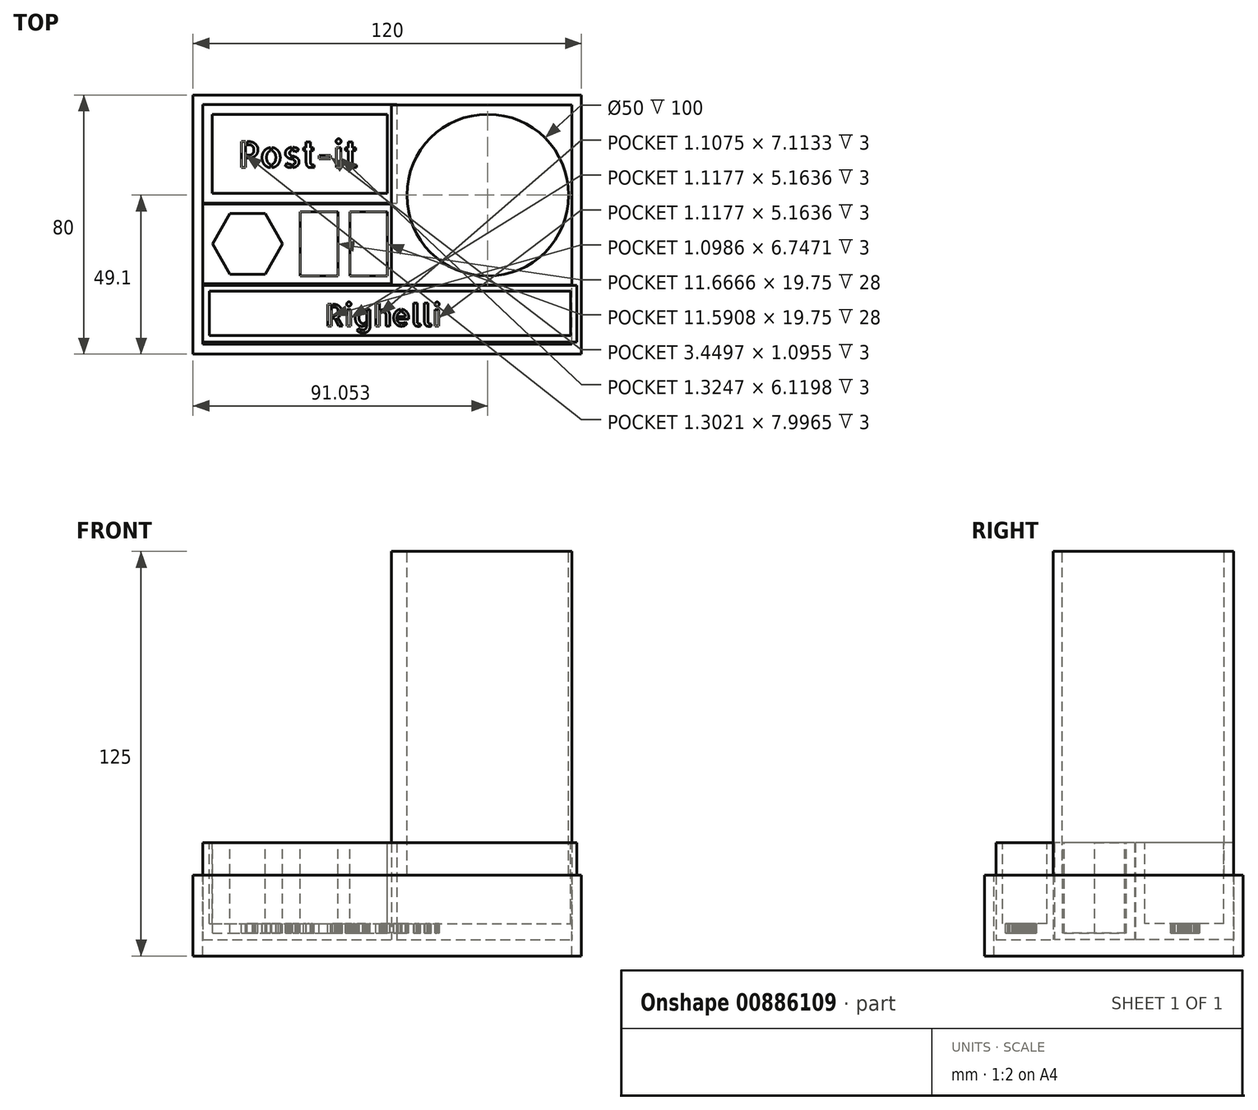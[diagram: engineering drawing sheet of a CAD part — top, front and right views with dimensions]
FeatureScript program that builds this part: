
annotation { "Feature Type Name" : "Feature", "Feature Type Description" : "" }
export const myFeature = defineFeature(function(context is Context, id is Id, definition is map)
    precondition{}
    {
        {
            var Q0;
            Q0=qCreatedBy(makeId("Top.planeOp"),FACE);
            var sketch = newSketch(context, id + "F0", { "sketchPlane" : qUnion([Q0])});
            skLineSegment(sketch, "E0.bottom", {"start": v(-60, 40) * mm, "end": v(60, 40) * mm});
            skLineSegment(sketch, "E0.top", {"start": v(-60, -40) * mm, "end": v(60, -40) * mm});
            skLineSegment(sketch, "E0.left", {"start": v(-60, 40) * mm, "end": v(-60, -40) * mm});
            skLineSegment(sketch, "E0.right", {"start": v(60, 40) * mm, "end": v(60, -40) * mm});
            skSolve(sketch);
        }
        {
            var Q0;
            Q0=qSketchRegion(id+"F0",true);
            extrude(context, id + "F1", {"entities" : qUnion([Q0]), "depth" : 25 * mm, "offsetDistance" : 25 * mm});
        }
        {
            var Q0;
            Q0=makeQuery(id+"F1.opExtrude","CAP_FACE",FACE,{"disambiguationData":[OSD([sQuery(id+"F0.wireOp",EDGE,"E0.bottom"),sQuery(id+"F0.wireOp",EDGE,"E0.top"),sQuery(id+"F0.wireOp",EDGE,"E0.left"),sQuery(id+"F0.wireOp",EDGE,"E0.right")])],"isStart":false});
            var sketch = newSketch(context, id + "F2", { "sketchPlane" : qUnion([Q0])});
            skLineSegment(sketch, "E1.bottom", {"start": v(-57, 37) * mm, "end": v(57, 37) * mm});
            skLineSegment(sketch, "E1.top", {"start": v(-57, -37) * mm, "end": v(57, -37) * mm});
            skLineSegment(sketch, "E1.left", {"start": v(-57, 37) * mm, "end": v(-57, -37) * mm});
            skLineSegment(sketch, "E1.right", {"start": v(57, 37) * mm, "end": v(57, -37) * mm});
            skSolve(sketch);
        }
        {
            var Q0;
            Q0=makeQuery(id+"F2.imprint","IMPRINT",FACE,{"disambiguationData":[TD([[makeQuery(id+"F2.imprint","IMPRINT",EDGE,{"derivedFrom":sQuery(id+"F2.wireOp",EDGE,"E1.bottom")}),-1.0]])]});
            extrude(context, id + "F3", {"entities" : qUnion([Q0]), "operationType" : NewBodyOperationType.REMOVE, "oppositeDirection" : true, "depth" : 20 * mm, "offsetDistance" : 25 * mm});
        }
        {
            var Q0;
            Q0=makeQuery(id+"F3.boolean.opBoolean","COPY",FACE,{"derivedFrom":makeQuery(id+"F3.opExtrude","CAP_FACE",FACE,{"disambiguationData":[OSD([sQuery(id+"F2.wireOp",EDGE,"E1.bottom"),sQuery(id+"F2.wireOp",EDGE,"E1.top"),sQuery(id+"F2.wireOp",EDGE,"E1.left"),sQuery(id+"F2.wireOp",EDGE,"E1.right")])],"isStart":false})});
            var sketch = newSketch(context, id + "F4", { "sketchPlane" : qUnion([Q0])});
            skLineSegment(sketch, "E2.bottom", {"start": v(57, 37) * mm, "end": v(1.35, 37) * mm});
            skLineSegment(sketch, "E2.top", {"start": v(57, -18.68) * mm, "end": v(1.35, -18.68) * mm});
            skLineSegment(sketch, "E2.left", {"start": v(57, 37) * mm, "end": v(57, -18.68) * mm});
            skLineSegment(sketch, "E2.right", {"start": v(1.35, 37) * mm, "end": v(1.35, -18.68) * mm});
            skSolve(sketch);
        }
        {
            var Q0;
            Q0=makeQuery(id+"F4.imprint","IMPRINT",FACE,{"disambiguationData":[TD([[makeQuery(id+"F4.imprint","IMPRINT",EDGE,{"derivedFrom":sQuery(id+"F4.wireOp",EDGE,"E2.bottom")}),-1.0]])]});
            var sketch = newSketch(context, id + "F5", { "sketchPlane" : qUnion([Q0])});
            skSolve(sketch);
        }
        {
            var Q0;
            Q0=makeQuery(id+"F5.imprint","IMPRINT",FACE,{"disambiguationData":[TD([[makeQuery(id+"F5.imprint","IMPRINT",EDGE,{"derivedFrom":makeQuery(id+"F4.imprint","IMPRINT",EDGE,{"derivedFrom":sQuery(id+"F4.wireOp",EDGE,"E2.bottom")})}),-1.0]])]});
            extrude(context, id + "F6", {"entities" : qUnion([Q0]), "operationType" : NewBodyOperationType.ADD, "depth" : 120 * mm, "offsetDistance" : 25 * mm});
        }
        {
            var Q0;
            Q0=makeQuery(id+"F6.opExtrude","CAP_FACE",FACE,{"disambiguationData":[OSD([sQuery(id+"F4.wireOp",EDGE,"E2.bottom"),sQuery(id+"F4.wireOp",EDGE,"E2.top"),sQuery(id+"F4.wireOp",EDGE,"E2.left"),sQuery(id+"F4.wireOp",EDGE,"E2.right")])],"isStart":false});
            var sketch = newSketch(context, id + "F7", { "sketchPlane" : qUnion([Q0])});
            skCircle(sketch, "E3", {"center": v(31.05, 9.1) * mm, "radius": 25 * mm});
            skSolve(sketch);
        }
        {
            var Q0;
            Q0=qSketchRegion(id+"F2",true);
            var Q1;
            Q1=qSketchRegion(id+"F7",true);
            extrude(context, id + "F8", {"entities" : qUnion([Q0, Q1]), "operationType" : NewBodyOperationType.REMOVE, "oppositeDirection" : true, "depth" : 116 * mm, "offsetDistance" : 25 * mm});
        }
        {
            var Q0;
            {var subQ4=sQuery(id+"F4.wireOp",EDGE,"E2.top");Q0=makeQuery(id+"F4.imprint","IMPRINT",FACE,{"disambiguationData":[TD([[makeQuery(id+"F4.imprint","IMPRINT",EDGE,{"derivedFrom":subQ4}),1.0]])]});}
            var sketch = newSketch(context, id + "F9", { "sketchPlane" : qUnion([Q0])});
            skLineSegment(sketch, "E4.bottom", {"start": v(-57.04, 37.04) * mm, "end": v(2.94, 37.04) * mm});
            skLineSegment(sketch, "E4.top", {"start": v(-57.04, 6.65) * mm, "end": v(2.94, 6.65) * mm});
            skLineSegment(sketch, "E4.left", {"start": v(-57.04, 37.04) * mm, "end": v(-57.04, 6.65) * mm});
            skLineSegment(sketch, "E4.right", {"start": v(2.94, 37.04) * mm, "end": v(2.94, 6.65) * mm});
            skSolve(sketch);
        }
        {
            var Q0;
            Q0=qSketchRegion(id+"F9",true);
            extrude(context, id + "F10", {"entities" : qUnion([Q0]), "depth" : 30 * mm, "offsetDistance" : 25 * mm});
        }
        {
            var Q0;
            Q0=makeQuery(id+"F10.opExtrude","CAP_FACE",FACE,{"disambiguationData":[OSD([sQuery(id+"F9.wireOp",EDGE,"E4.bottom"),sQuery(id+"F9.wireOp",EDGE,"E4.top"),sQuery(id+"F9.wireOp",EDGE,"E4.left"),sQuery(id+"F9.wireOp",EDGE,"E4.right")])],"isStart":false});
            var sketch = newSketch(context, id + "F11", { "sketchPlane" : qUnion([Q0])});
            skLineSegment(sketch, "E5.bottom", {"start": v(-54.04, 34.04) * mm, "end": v(0, 34.04) * mm});
            skLineSegment(sketch, "E5.top", {"start": v(-54.04, 9.65) * mm, "end": v(0, 9.65) * mm});
            skLineSegment(sketch, "E5.left", {"start": v(-54.04, 34.04) * mm, "end": v(-54.04, 9.65) * mm});
            skLineSegment(sketch, "E5.right", {"start": v(0, 34.04) * mm, "end": v(0, 9.65) * mm});
            skSolve(sketch);
        }
        {
            var Q0;
            Q0=makeQuery(id+"F11.imprint","IMPRINT",FACE,{"disambiguationData":[TD([[makeQuery(id+"F11.imprint","IMPRINT",EDGE,{"derivedFrom":sQuery(id+"F11.wireOp",EDGE,"E5.bottom")}),-1.0]])]});
            extrude(context, id + "F12", {"entities" : qUnion([Q0]), "operationType" : NewBodyOperationType.REMOVE, "oppositeDirection" : true, "depth" : 25 * mm, "offsetDistance" : 25 * mm});
        }
        {
            var Q0;
            {var subQ4=sQuery(id+"F4.wireOp",EDGE,"E2.top");Q0=makeQuery(id+"F4.imprint","IMPRINT",FACE,{"disambiguationData":[TD([[makeQuery(id+"F4.imprint","IMPRINT",EDGE,{"derivedFrom":subQ4}),1.0]])]});}
            var sketch = newSketch(context, id + "F13", { "sketchPlane" : qUnion([Q0])});
            skLineSegment(sketch, "E6.bottom", {"start": v(-57, 6.41) * mm, "end": v(1.35, 6.41) * mm});
            skLineSegment(sketch, "E6.top", {"start": v(-57, -18.34) * mm, "end": v(1.35, -18.34) * mm});
            skLineSegment(sketch, "E6.left", {"start": v(-57, 6.41) * mm, "end": v(-57, -18.34) * mm});
            skLineSegment(sketch, "E6.right", {"start": v(1.35, 6.41) * mm, "end": v(1.35, -18.34) * mm});
            skSolve(sketch);
        }
        {
            var Q0;
            Q0=qSketchRegion(id+"F13",true);
            extrude(context, id + "F14", {"entities" : qUnion([Q0]), "depth" : 30 * mm, "offsetDistance" : 25 * mm});
        }
        {
            var Q0;
            Q0=makeQuery(id+"F14.opExtrude","CAP_FACE",FACE,{"disambiguationData":[OSD([sQuery(id+"F13.wireOp",EDGE,"E6.bottom"),sQuery(id+"F13.wireOp",EDGE,"E6.top"),sQuery(id+"F13.wireOp",EDGE,"E6.left"),sQuery(id+"F13.wireOp",EDGE,"E6.right")])],"isStart":false});
            var sketch = newSketch(context, id + "F15", { "sketchPlane" : qUnion([Q0])});
            skCircle(sketch, "E7.cCircle", {"center": v(-43.17, -5.96) * mm, "radius": 9.38 * mm, "construction": true});
            skLineSegment(sketch, "E7.0", {"start": v(-48.59, 3.41) * mm, "end": v(-37.76, 3.41) * mm});
            skLineSegment(sketch, "E7.1", {"start": v(-37.76, 3.41) * mm, "end": v(-32.35, -5.96) * mm});
            skLineSegment(sketch, "E7.2", {"start": v(-32.35, -5.96) * mm, "end": v(-37.76, -15.34) * mm});
            skLineSegment(sketch, "E7.3", {"start": v(-37.76, -15.34) * mm, "end": v(-48.59, -15.34) * mm});
            skLineSegment(sketch, "E7.4", {"start": v(-48.59, -15.34) * mm, "end": v(-54, -5.96) * mm});
            skLineSegment(sketch, "E7.5", {"start": v(-54, -5.96) * mm, "end": v(-48.59, 3.41) * mm});
            skPoint(sketch, "E7.0.midPoint", {"position": v(-43.17, 3.41) * mm});
            skSolve(sketch);
        }
        {
            var Q0;
            Q0=qSketchRegion(id+"F15",true);
            extrude(context, id + "F16", {"entities" : qUnion([Q0]), "operationType" : NewBodyOperationType.REMOVE, "oppositeDirection" : true, "depth" : 28 * mm, "offsetDistance" : 25 * mm});
        }
        {
            var Q0;
            Q0=makeQuery(id+"F15.imprint","IMPRINT",FACE,{"disambiguationData":[TD([[makeQuery(id+"F15.imprint","IMPRINT",EDGE,{"derivedFrom":sQuery(id+"F15.wireOp",EDGE,"E7.0")}),-1.0]])]});
            extrude(context, id + "F17", {"entities" : qUnion([Q0]), "operationType" : NewBodyOperationType.REMOVE, "oppositeDirection" : true, "depth" : 28 * mm, "offsetDistance" : 25 * mm});
        }
        {
            var Q0;
            Q0=makeQuery(id+"F14.opExtrude","CAP_FACE",FACE,{"disambiguationData":[OSD([sQuery(id+"F13.wireOp",EDGE,"E6.bottom"),sQuery(id+"F13.wireOp",EDGE,"E6.top"),sQuery(id+"F13.wireOp",EDGE,"E6.left"),sQuery(id+"F13.wireOp",EDGE,"E6.right")])],"isStart":false});
            var sketch = newSketch(context, id + "F18", { "sketchPlane" : qUnion([Q0])});
            skLineSegment(sketch, "E8.bottom", {"start": v(-26.87, 3.91) * mm, "end": v(-15.2, 3.91) * mm});
            skLineSegment(sketch, "E8.top", {"start": v(-26.87, -15.84) * mm, "end": v(-15.2, -15.84) * mm});
            skLineSegment(sketch, "E8.left", {"start": v(-26.87, 3.91) * mm, "end": v(-26.87, -15.84) * mm});
            skLineSegment(sketch, "E8.right", {"start": v(-15.2, 3.91) * mm, "end": v(-15.2, -15.84) * mm});
            skSolve(sketch);
        }
        {
            var Q0;
            Q0=makeQuery(id+"F18.imprint","IMPRINT",FACE,{"disambiguationData":[TD([[makeQuery(id+"F18.imprint","IMPRINT",EDGE,{"derivedFrom":sQuery(id+"F18.wireOp",EDGE,"E8.bottom")}),-1.0]])]});
            extrude(context, id + "F19", {"entities" : qUnion([Q0]), "operationType" : NewBodyOperationType.REMOVE, "oppositeDirection" : true, "depth" : 28 * mm, "offsetDistance" : 25 * mm});
        }
        {
            var Q0;
            Q0=makeQuery(id+"F14.opExtrude","CAP_FACE",FACE,{"disambiguationData":[OSD([sQuery(id+"F13.wireOp",EDGE,"E6.bottom"),sQuery(id+"F13.wireOp",EDGE,"E6.top"),sQuery(id+"F13.wireOp",EDGE,"E6.left"),sQuery(id+"F13.wireOp",EDGE,"E6.right")])],"isStart":false});
            var sketch = newSketch(context, id + "F20", { "sketchPlane" : qUnion([Q0])});
            skLineSegment(sketch, "E9.bottom", {"start": v(-11.6, 3.91) * mm, "end": v(0, 3.91) * mm});
            skLineSegment(sketch, "E9.top", {"start": v(-11.6, -15.84) * mm, "end": v(0, -15.84) * mm});
            skLineSegment(sketch, "E9.left", {"start": v(-11.6, 3.91) * mm, "end": v(-11.6, -15.84) * mm});
            skLineSegment(sketch, "E9.right", {"start": v(0, 3.91) * mm, "end": v(0, -15.84) * mm});
            skSolve(sketch);
        }
        {
            var Q0;
            Q0=qSketchRegion(id+"F20",true);
            extrude(context, id + "F21", {"entities" : qUnion([Q0]), "operationType" : NewBodyOperationType.REMOVE, "oppositeDirection" : true, "depth" : 28 * mm, "offsetDistance" : 25 * mm});
        }
        {
            var Q0;
            {var subQ4=sQuery(id+"F4.wireOp",EDGE,"E2.top");Q0=makeQuery(id+"F4.imprint","IMPRINT",FACE,{"disambiguationData":[TD([[makeQuery(id+"F4.imprint","IMPRINT",EDGE,{"derivedFrom":subQ4}),1.0]])]});}
            var sketch = newSketch(context, id + "F22", { "sketchPlane" : qUnion([Q0])});
            skLineSegment(sketch, "E10.bottom", {"start": v(-57.04, -18.79) * mm, "end": v(58.61, -18.79) * mm});
            skLineSegment(sketch, "E10.top", {"start": v(-57.04, -36.34) * mm, "end": v(58.61, -36.34) * mm});
            skLineSegment(sketch, "E10.left", {"start": v(-57.04, -18.79) * mm, "end": v(-57.04, -36.34) * mm});
            skLineSegment(sketch, "E10.right", {"start": v(58.61, -18.79) * mm, "end": v(58.61, -36.34) * mm});
            skSolve(sketch);
        }
        {
            var Q0;
            Q0=qSketchRegion(id+"F22",true);
            extrude(context, id + "F23", {"entities" : qUnion([Q0]), "operationType" : NewBodyOperationType.ADD, "depth" : 30 * mm, "offsetDistance" : 25 * mm});
        }
        {
            var Q0;
            Q0=makeQuery(id+"F23.opExtrude","CAP_FACE",FACE,{"disambiguationData":[OSD([sQuery(id+"F22.wireOp",EDGE,"E10.bottom"),sQuery(id+"F22.wireOp",EDGE,"E10.top"),sQuery(id+"F22.wireOp",EDGE,"E10.left"),sQuery(id+"F22.wireOp",EDGE,"E10.right")])],"isStart":false});
            var sketch = newSketch(context, id + "F24", { "sketchPlane" : qUnion([Q0])});
            skLineSegment(sketch, "E11.bottom", {"start": v(-55.04, -20.59) * mm, "end": v(56.61, -20.59) * mm});
            skLineSegment(sketch, "E11.top", {"start": v(-55.04, -34.34) * mm, "end": v(56.61, -34.34) * mm});
            skLineSegment(sketch, "E11.left", {"start": v(-55.04, -20.59) * mm, "end": v(-55.04, -34.34) * mm});
            skLineSegment(sketch, "E11.right", {"start": v(56.61, -20.59) * mm, "end": v(56.61, -34.34) * mm});
            skSolve(sketch);
        }
        {
            var Q0;
            Q0=qSketchRegion(id+"F24",true);
            extrude(context, id + "F25", {"entities" : qUnion([Q0]), "operationType" : NewBodyOperationType.REMOVE, "oppositeDirection" : true, "depth" : 25 * mm, "offsetDistance" : 25 * mm});
        }
        {
            var Q0;
            Q0=makeQuery(id+"F25.boolean.opBoolean","COPY",FACE,{"derivedFrom":makeQuery(id+"F25.opExtrude","CAP_FACE",FACE,{"disambiguationData":[OSD([sQuery(id+"F24.wireOp",EDGE,"E11.bottom"),sQuery(id+"F24.wireOp",EDGE,"E11.top"),sQuery(id+"F24.wireOp",EDGE,"E11.left"),sQuery(id+"F24.wireOp",EDGE,"E11.right")])],"isStart":false})});
            var sketch = newSketch(context, id + "F26", { "sketchPlane" : qUnion([Q0])});
            skText(sketch, "E12", { "text": "Righelli", "fontName": "AllertaStencil-Regular.ttf"});
            const initialGuessF26  = {"E12": [-0.01924, -0.03139, 1, 0, 0.00675]};
            skSetInitialGuess(sketch, initialGuessF26);
            skSolve(sketch);
        }
        {
            var Q0;
            Q0=qSketchRegion(id+"F26",true);
            extrude(context, id + "F27", {"entities" : qUnion([Q0]), "operationType" : NewBodyOperationType.REMOVE, "oppositeDirection" : true, "depth" : 3 * mm, "offsetDistance" : 25 * mm});
        }
        {
            var Q0;
            Q0=makeQuery(id+"F12.boolean.opBoolean","COPY",FACE,{"derivedFrom":makeQuery(id+"F12.opExtrude","CAP_FACE",FACE,{"disambiguationData":[OSD([sQuery(id+"F11.wireOp",EDGE,"E5.bottom"),sQuery(id+"F11.wireOp",EDGE,"E5.top"),sQuery(id+"F11.wireOp",EDGE,"E5.left"),sQuery(id+"F11.wireOp",EDGE,"E5.right")])],"isStart":false})});
            var sketch = newSketch(context, id + "F28", { "sketchPlane" : qUnion([Q0])});
            skText(sketch, "E13", { "text": "Post-it", "fontName": "AllertaStencil-Regular.ttf"});
            const initialGuessF28  = {"E13": [-0.04604, 0.01765, 1, 0, 0.008]};
            skSetInitialGuess(sketch, initialGuessF28);
            skSolve(sketch);
        }
        {
            var Q0;
            Q0=qSketchRegion(id+"F28",true);
            extrude(context, id + "F29", {"entities" : qUnion([Q0]), "operationType" : NewBodyOperationType.REMOVE, "oppositeDirection" : true, "depth" : 3 * mm, "offsetDistance" : 25 * mm});
        }
        {
            var Q0;
            Q0=qSketchRegion(id+"F7",true);
            extrude(context, id + "F30", {"entities" : qUnion([Q0]), "operationType" : NewBodyOperationType.REMOVE, "oppositeDirection" : true, "depth" : 116 * mm, "offsetDistance" : 25 * mm});
        }
    });
